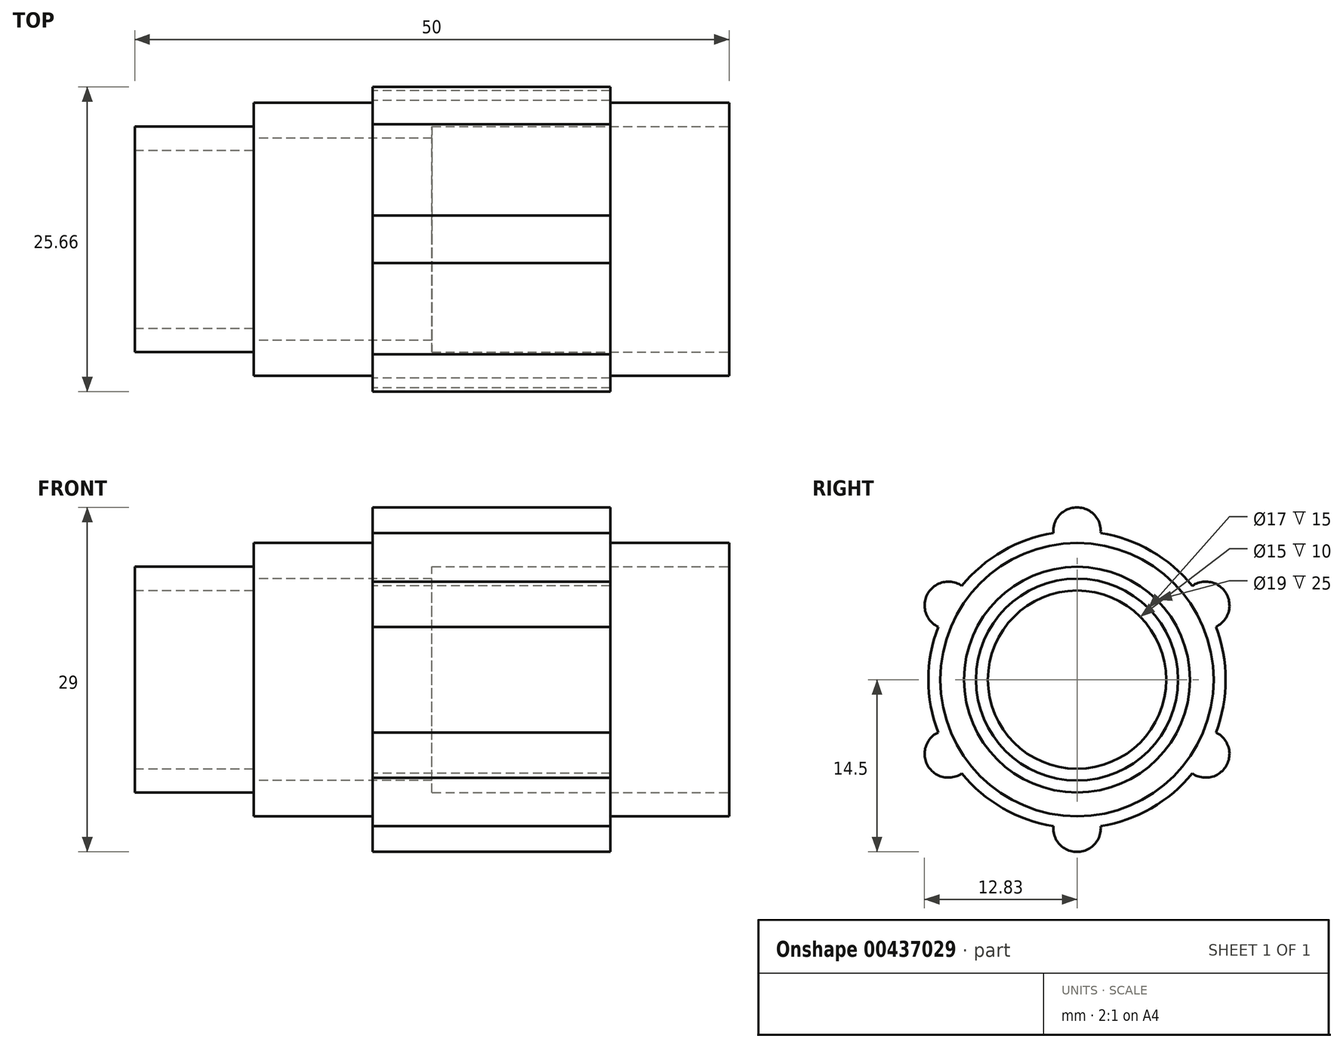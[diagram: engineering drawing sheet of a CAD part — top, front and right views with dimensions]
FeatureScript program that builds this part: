
annotation { "Feature Type Name" : "Feature", "Feature Type Description" : "" }
export const myFeature = defineFeature(function(context is Context, id is Id, definition is map)
    precondition{}
    {
        {
            var Q0;
            Q0=qCreatedBy(makeId("Right.planeOp"),FACE);
            var sketch = newSketch(context, id + "F0", { "sketchPlane" : qUnion([Q0])});
            skCircle(sketch, "E0", {"center": v(0, 0) * mm, "radius": 8.5 * mm});
            skCircle(sketch, "E1", {"center": v(0, 0) * mm, "radius": 12.5 * mm});
            skArc(sketch, "E2", {"start": v(-2, -12.34) * mm, "mid": v(0, -14.5) * mm, "end": v(2, -12.34) * mm});
            skArc(sketch, "E3.1.0", {"start": v(9.69, -7.9) * mm, "mid": v(12.56, -7.25) * mm, "end": v(11.68, -4.44) * mm});
            skArc(sketch, "E3.2.0", {"start": v(11.68, 4.44) * mm, "mid": v(12.56, 7.25) * mm, "end": v(9.69, 7.9) * mm});
            skArc(sketch, "E3.3.0", {"start": v(2, 12.34) * mm, "mid": v(0, 14.5) * mm, "end": v(-2, 12.34) * mm});
            skArc(sketch, "E3.4.0", {"start": v(-9.69, 7.9) * mm, "mid": v(-12.56, 7.25) * mm, "end": v(-11.68, 4.44) * mm});
            skArc(sketch, "E3.5.0", {"start": v(-11.68, -4.44) * mm, "mid": v(-12.56, -7.25) * mm, "end": v(-9.69, -7.9) * mm});
            skSolve(sketch);
        }
        {
            var Q0;
            Q0=qSketchRegion(id+"F0",true);
            extrude(context, id + "F1", {"entities" : qUnion([Q0]), "endBound" : BoundingType.SYMMETRIC, "depth" : 20 * mm});
        }
        {
            var Q0;
            Q0=qCreatedBy(makeId("Right.planeOp"),FACE);
            var sketch = newSketch(context, id + "F2", { "sketchPlane" : qUnion([Q0])});
            skCircle(sketch, "E4", {"center": v(0, 0) * mm, "radius": 8.5 * mm});
            skCircle(sketch, "E5", {"center": v(0, 0) * mm, "radius": 11.5 * mm});
            skSolve(sketch);
        }
        {
            var Q0;
            Q0=qSketchRegion(id+"F2",true);
            extrude(context, id + "F3", {"entities" : qUnion([Q0]), "operationType" : NewBodyOperationType.ADD, "endBound" : BoundingType.SYMMETRIC, "depth" : 40 * mm});
        }
        {
            var Q0;
            Q0=makeQuery(id+"F3.opExtrude","CAP_FACE",FACE,{"disambiguationData":[OSD([sQuery(id+"F2.wireOp",EDGE,"E4"),sQuery(id+"F2.wireOp",EDGE,"E5")])],"isStart":true});
            var sketch = newSketch(context, id + "F4", { "sketchPlane" : qUnion([Q0])});
            skCircle(sketch, "E6", {"center": v(0, 0) * mm, "radius": 9.5 * mm});
            skCircle(sketch, "E7", {"center": v(0, 0) * mm, "radius": 7.5 * mm});
            skSolve(sketch);
        }
        {
            var Q0;
            Q0=qSketchRegion(id+"F4",true);
            extrude(context, id + "F5", {"entities" : qUnion([Q0]), "operationType" : NewBodyOperationType.ADD, "depth" : 10 * mm});
        }
        {
            var Q0;
            Q0=makeQuery(id+"F3.opExtrude","CAP_FACE",FACE,{"disambiguationData":[OSD([sQuery(id+"F2.wireOp",EDGE,"E4"),sQuery(id+"F2.wireOp",EDGE,"E5")])],"isStart":false});
            var sketch = newSketch(context, id + "F6", { "sketchPlane" : qUnion([Q0])});
            skCircle(sketch, "E8", {"center": v(0, 0) * mm, "radius": 9.5 * mm});
            skSolve(sketch);
        }
        {
            var Q0;
            Q0=qSketchRegion(id+"F6",true);
            extrude(context, id + "F7", {"entities" : qUnion([Q0]), "operationType" : NewBodyOperationType.REMOVE, "oppositeDirection" : true, "depth" : 25 * mm});
        }
    });
